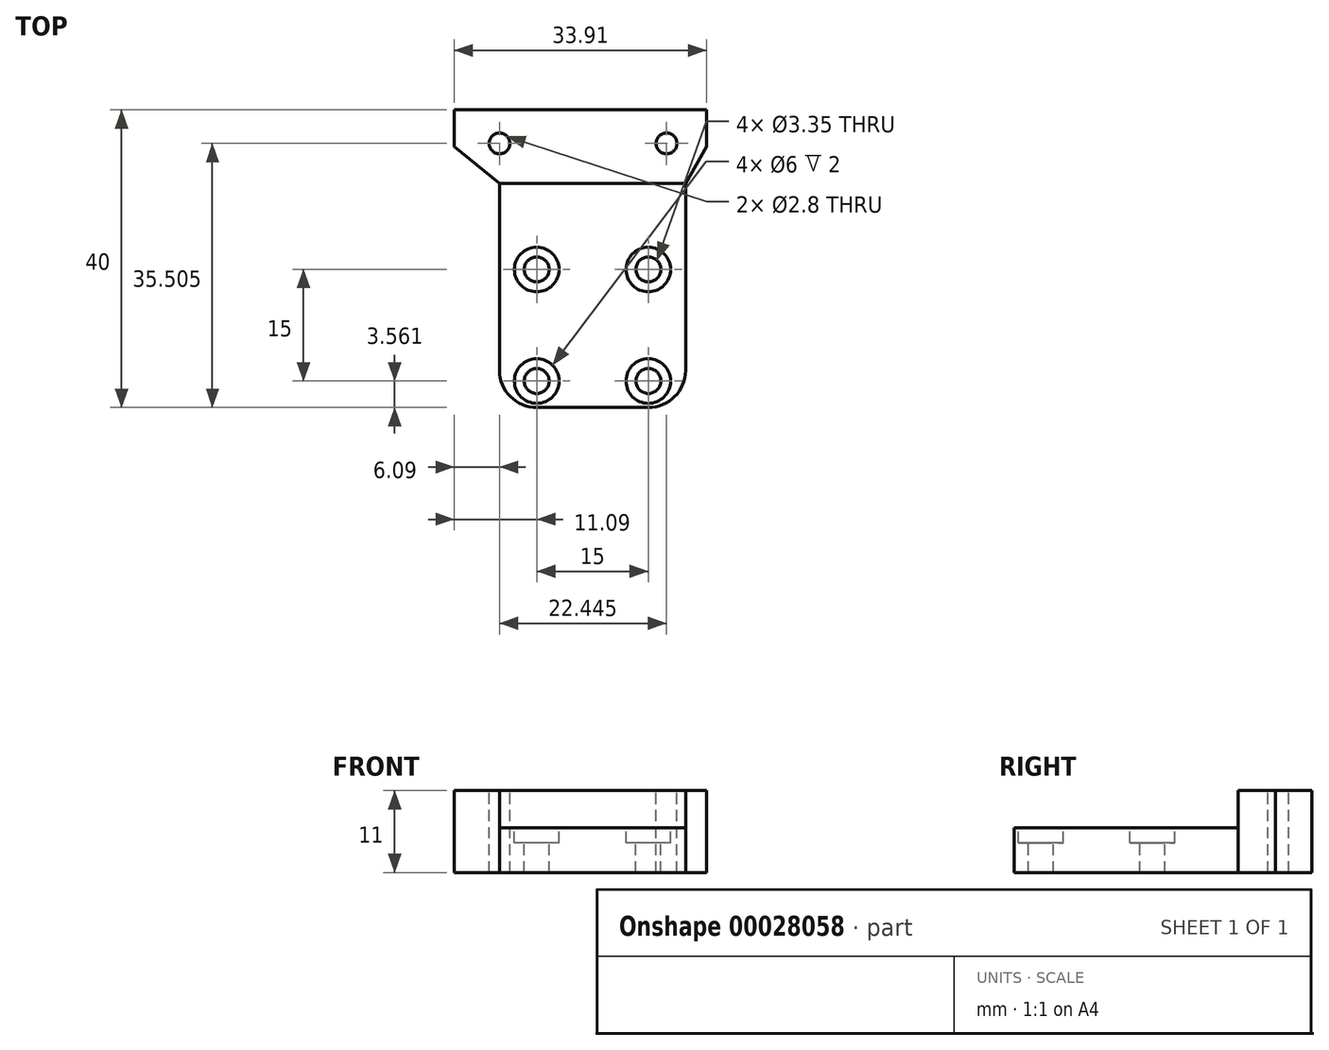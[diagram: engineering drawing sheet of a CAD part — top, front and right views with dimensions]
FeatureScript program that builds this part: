
annotation { "Feature Type Name" : "Feature", "Feature Type Description" : "" }
export const myFeature = defineFeature(function(context is Context, id is Id, definition is map)
    precondition{}
    {
        {
            var Q0;
            Q0=qCreatedBy(makeId("Top.planeOp"),FACE);
            var sketch = newSketch(context, id + "F0", { "sketchPlane" : qUnion([Q0])});
            skLineSegment(sketch, "E0.bottom", {"start": v(0, 0) * mm, "end": v(25, 0) * mm});
            skLineSegment(sketch, "E0.top", {"start": v(-6.1, 40) * mm, "end": v(27.82, 40) * mm});
            skLineSegment(sketch, "E1", {"start": v(0, 30.1) * mm, "end": v(25, 30.1) * mm});
            skLineSegment(sketch, "E2", {"start": v(-6.1, 35.1) * mm, "end": v(27.82, 35.1) * mm});
            skLineSegment(sketch, "E3", {"start": v(0, 0) * mm, "end": v(0, 30.1) * mm});
            skLineSegment(sketch, "E4", {"start": v(0, 30.1) * mm, "end": v(-6.1, 35.1) * mm});
            skLineSegment(sketch, "E5", {"start": v(-6.1, 35.1) * mm, "end": v(-6.1, 40) * mm});
            skLineSegment(sketch, "E6", {"start": v(25, 0) * mm, "end": v(25, 30.1) * mm});
            skLineSegment(sketch, "E7", {"start": v(25, 30.1) * mm, "end": v(27.82, 35.1) * mm});
            skLineSegment(sketch, "E8", {"start": v(27.82, 35.1) * mm, "end": v(27.82, 40) * mm});
            skSolve(sketch);
        }
        {
            var Q0;
            Q0=qSketchRegion(id+"F0",true);
            extrude(context, id + "F1", {"entities" : qUnion([Q0]), "depth" : 6 * mm});
        }
        {
            var Q0;
            Q0=makeQuery(id+"F1.opExtrude","CAP_FACE",FACE,{"disambiguationData":[OSD([sQuery(id+"F0.wireOp",EDGE,"E0.bottom"),sQuery(id+"F0.wireOp",EDGE,"E0.top"),sQuery(id+"F0.wireOp",EDGE,"E3"),sQuery(id+"F0.wireOp",EDGE,"E4"),sQuery(id+"F0.wireOp",EDGE,"E5"),sQuery(id+"F0.wireOp",EDGE,"E6"),sQuery(id+"F0.wireOp",EDGE,"E7"),sQuery(id+"F0.wireOp",EDGE,"E8")])],"isStart":false});
            var sketch = newSketch(context, id + "F2", { "sketchPlane" : qUnion([Q0])});
            skCircle(sketch, "E9", {"center": v(5, 18.56) * mm, "radius": 1.68 * mm});
            skCircle(sketch, "E10", {"center": v(20, 18.56) * mm, "radius": 1.68 * mm});
            skCircle(sketch, "E11", {"center": v(5, 3.56) * mm, "radius": 1.68 * mm});
            skCircle(sketch, "E12", {"center": v(20, 3.56) * mm, "radius": 1.68 * mm});
            skLineSegment(sketch, "E13", {"start": v(5, 18.56) * mm, "end": v(0, 18.56) * mm});
            skLineSegment(sketch, "E14", {"start": v(20, 3.56) * mm, "end": v(25, 3.56) * mm});
            skCircle(sketch, "E15", {"center": v(5, 18.56) * mm, "radius": 3 * mm});
            skCircle(sketch, "E16", {"center": v(20, 18.56) * mm, "radius": 3 * mm});
            skCircle(sketch, "E17", {"center": v(5, 3.56) * mm, "radius": 3 * mm});
            skCircle(sketch, "E18", {"center": v(20, 3.56) * mm, "radius": 3 * mm});
            skSolve(sketch);
        }
        {
            var Q0;
            Q0=makeQuery(id+"F2.imprint","IMPRINT",FACE,{"disambiguationData":[TD([[makeQuery(id+"F2.imprint","IMPRINT",EDGE,{"derivedFrom":sQuery(id+"F2.wireOp",EDGE,"E9")}),1.0]])]});
            var Q1;
            Q1=makeQuery(id+"F2.imprint","IMPRINT",FACE,{"disambiguationData":[TD([[makeQuery(id+"F2.imprint","IMPRINT",EDGE,{"derivedFrom":sQuery(id+"F2.wireOp",EDGE,"E10")}),1.0]])]});
            var Q2;
            Q2=makeQuery(id+"F2.imprint","IMPRINT",FACE,{"disambiguationData":[TD([[makeQuery(id+"F2.imprint","IMPRINT",EDGE,{"derivedFrom":sQuery(id+"F2.wireOp",EDGE,"E12")}),1.0]])]});
            var Q3;
            Q3=makeQuery(id+"F2.imprint","IMPRINT",FACE,{"disambiguationData":[TD([[makeQuery(id+"F2.imprint","IMPRINT",EDGE,{"derivedFrom":sQuery(id+"F2.wireOp",EDGE,"E11")}),1.0]])]});
            var Q4;
            Q4=makeQuery(id+"F2.imprint","IMPRINT",FACE,{"disambiguationData":[TD([[makeQuery(id+"F2.imprint","IMPRINT",EDGE,{"derivedFrom":sQuery(id+"F2.wireOp",EDGE,"97d24b09-4827-4c46-a1fd-a3ea8677536d")}),1.0]])]});
            var Q5;
            Q5=makeQuery(id+"F2.imprint","IMPRINT",FACE,{"disambiguationData":[TD([[makeQuery(id+"F2.imprint","IMPRINT",EDGE,{"derivedFrom":sQuery(id+"F2.wireOp",EDGE,"b6eb7b6f-8bb0-4363-9520-a6d7085f5256")}),1.0]])]});
            extrude(context, id + "F3", {"entities" : qUnion([Q0, Q1, Q2, Q3, Q4, Q5]), "operationType" : NewBodyOperationType.REMOVE, "oppositeDirection" : true, "depth" : 25 * mm});
        }
        {
            var Q0;
            Q0=makeQuery(id+"F2.imprint","IMPRINT",FACE,{"disambiguationData":[TD([[makeQuery(id+"F2.imprint","IMPRINT",EDGE,{"derivedFrom":sQuery(id+"F2.wireOp",EDGE,"E9")}),-1.0]])]});
            var Q1;
            Q1=makeQuery(id+"F2.imprint","IMPRINT",FACE,{"disambiguationData":[TD([[makeQuery(id+"F2.imprint","IMPRINT",EDGE,{"derivedFrom":sQuery(id+"F2.wireOp",EDGE,"E10")}),-1.0]])]});
            var Q2;
            Q2=makeQuery(id+"F2.imprint","IMPRINT",FACE,{"disambiguationData":[TD([[makeQuery(id+"F2.imprint","IMPRINT",EDGE,{"derivedFrom":sQuery(id+"F2.wireOp",EDGE,"E12")}),-1.0]])]});
            var Q3;
            Q3=makeQuery(id+"F2.imprint","IMPRINT",FACE,{"disambiguationData":[TD([[makeQuery(id+"F2.imprint","IMPRINT",EDGE,{"derivedFrom":sQuery(id+"F2.wireOp",EDGE,"E11")}),-1.0]])]});
            extrude(context, id + "F4", {"entities" : qUnion([Q0, Q1, Q2, Q3]), "operationType" : NewBodyOperationType.REMOVE, "oppositeDirection" : true, "depth" : 2 * mm});
        }
        {
            var Q0;
            Q0=makeQuery(id+"F1.opExtrude","SWEPT_EDGE",EDGE,{"disambiguationData":[OSD([sQuery(id+"F0.wireOp",EDGE,"E0.bottom"),sQuery(id+"F0.wireOp",EDGE,"E0.left")])]});
            var Q1;
            Q1=makeQuery(id+"F1.opExtrude","SWEPT_EDGE",EDGE,{"disambiguationData":[OSD([sQuery(id+"F0.wireOp",EDGE,"E0.bottom"),sQuery(id+"F0.wireOp",EDGE,"E0.right")])]});
            fillet(context, id + "F5", {"entities" : qUnion([Q0, Q1]), "radius" : 5 * mm, "tangentPropagation" : true, "allowEdgeOverflow" : false});
        }
        {
            var Q0;
            Q0=makeQuery(id+"F0.imprint","IMPRINT",FACE,{"disambiguationData":[TD([[makeQuery(id+"F0.imprint","IMPRINT",EDGE,{"derivedFrom":sQuery(id+"F0.wireOp",EDGE,"E0.top")}),-1.0]])]});
            var Q1;
            Q1=makeQuery(id+"F0.imprint","IMPRINT",FACE,{"disambiguationData":[TD([[makeQuery(id+"F0.imprint","IMPRINT",EDGE,{"derivedFrom":sQuery(id+"F0.wireOp",EDGE,"E1")}),1.0]])]});
            extrude(context, id + "F6", {"entities" : qUnion([Q0, Q1]), "operationType" : NewBodyOperationType.ADD, "depth" : 11 * mm});
        }
        {
            var Q0;
            Q0=makeQuery(id+"F6.opExtrude","CAP_FACE",FACE,{"disambiguationData":[OSD([sQuery(id+"F0.wireOp",EDGE,"E0.top"),sQuery(id+"F0.wireOp",EDGE,"E1"),sQuery(id+"F0.wireOp",EDGE,"E4"),sQuery(id+"F0.wireOp",EDGE,"E5"),sQuery(id+"F0.wireOp",EDGE,"E7"),sQuery(id+"F0.wireOp",EDGE,"E8")])],"isStart":false});
            var sketch = newSketch(context, id + "F7", { "sketchPlane" : qUnion([Q0])});
            skCircle(sketch, "E19", {"center": v(22.45, 35.5) * mm, "radius": 1.4 * mm});
            skCircle(sketch, "E20", {"center": v(0, 35.5) * mm, "radius": 1.4 * mm});
            skSolve(sketch);
        }
        {
            var Q0;
            Q0=qSketchRegion(id+"F7",true);
            extrude(context, id + "F8", {"entities" : qUnion([Q0]), "operationType" : NewBodyOperationType.REMOVE, "endBound" : BoundingType.THROUGH_ALL, "oppositeDirection" : true, "depth" : 25 * mm});
        }
    });
